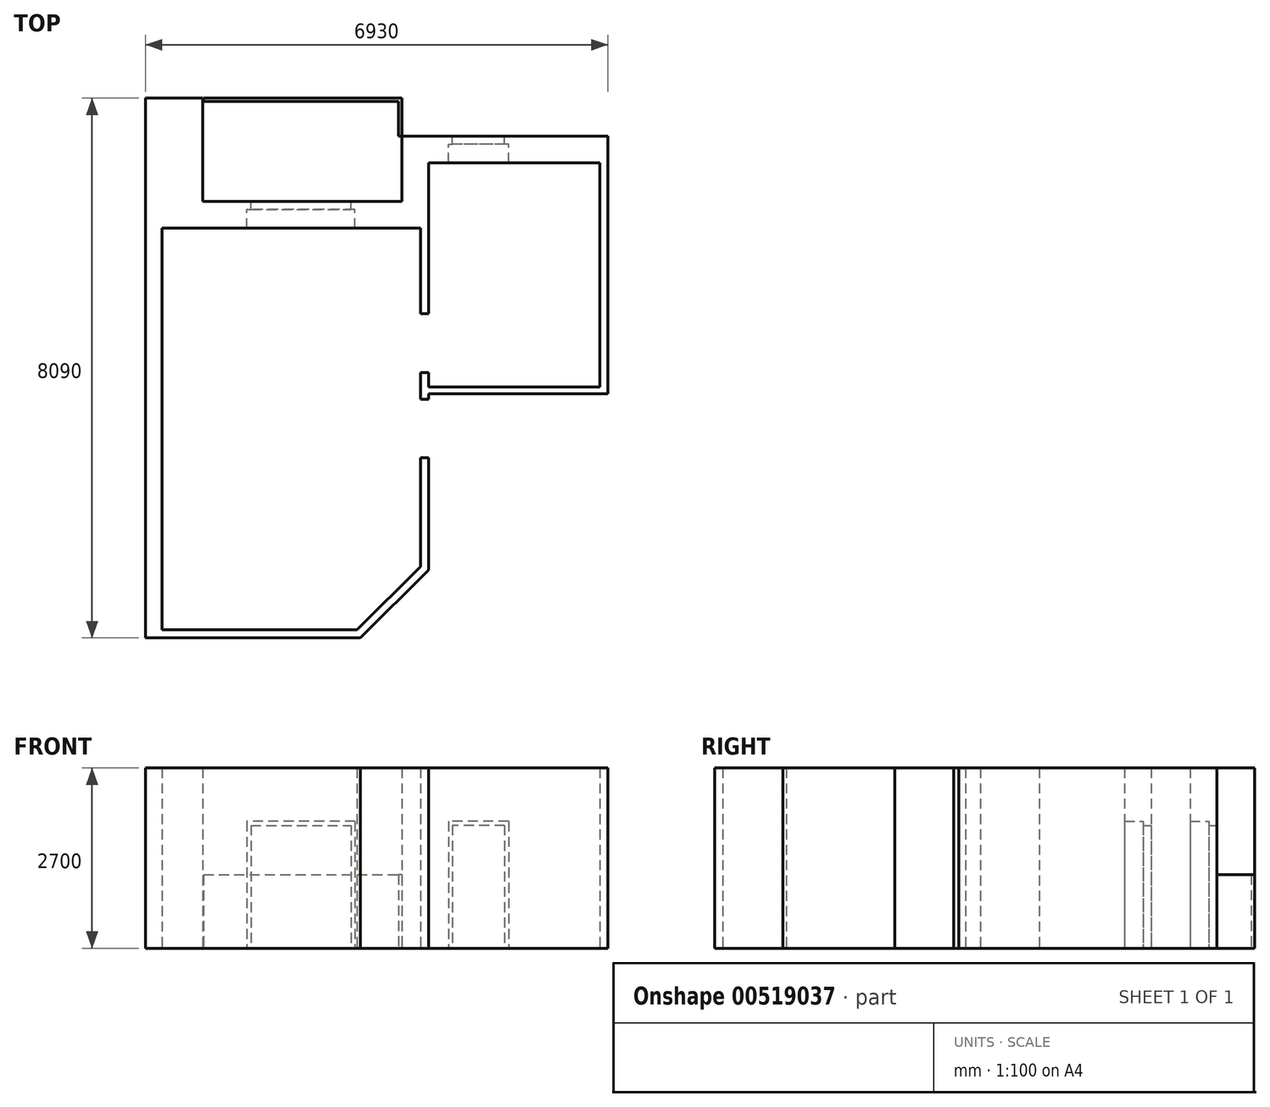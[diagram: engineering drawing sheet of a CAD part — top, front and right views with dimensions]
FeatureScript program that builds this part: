
annotation { "Feature Type Name" : "Feature", "Feature Type Description" : "" }
export const myFeature = defineFeature(function(context is Context, id is Id, definition is map)
    precondition{}
    {
        {
            var Q0;
            Q0=qCreatedBy(makeId("Top.planeOp"),FACE);
            var sketch = newSketch(context, id + "F0", { "sketchPlane" : qUnion([Q0])});
            skLineSegment(sketch, "E0", {"start": v(0, 0) * mm, "end": v(0, -6020) * mm, "construction": true});
            skLineSegment(sketch, "E1", {"start": v(0, -6020) * mm, "end": v(2920, -6020) * mm, "construction": true});
            skLineSegment(sketch, "E2", {"start": v(2920, -6020) * mm, "end": v(3870, -5070) * mm, "construction": true});
            skLineSegment(sketch, "E3", {"start": v(3870, -5070) * mm, "end": v(3870, 0) * mm, "construction": true});
            skLineSegment(sketch, "E4", {"start": v(3870, 0) * mm, "end": v(0, 0) * mm, "construction": true});
            skLineSegment(sketch, "E5.bottom", {"start": v(3990, 980) * mm, "end": v(6560, 980) * mm, "construction": true});
            skLineSegment(sketch, "E5.top", {"start": v(3990, -2380) * mm, "end": v(6560, -2380) * mm, "construction": true});
            skLineSegment(sketch, "E5.left", {"start": v(3990, 980) * mm, "end": v(3990, -2380) * mm, "construction": true});
            skLineSegment(sketch, "E5.right", {"start": v(6560, 980) * mm, "end": v(6560, -2380) * mm, "construction": true});
            skSolve(sketch);
        }
        {
            var Q0;
            Q0=qCreatedBy(makeId("Top.planeOp"),FACE);
            var sketch = newSketch(context, id + "F1", { "sketchPlane" : qUnion([Q0])});
            skLineSegment(sketch, "E6.0", {"start": v(0, 0) * mm, "end": v(0, -6020) * mm});
            skLineSegment(sketch, "E6.1", {"start": v(0, -6020) * mm, "end": v(2920, -6020) * mm});
            skLineSegment(sketch, "E6.2", {"start": v(2920, -6020) * mm, "end": v(3870, -5070) * mm});
            skLineSegment(sketch, "E6.3", {"start": v(3990, -2380) * mm, "end": v(6560, -2380) * mm});
            skLineSegment(sketch, "E6.4", {"start": v(6560, 980) * mm, "end": v(6560, -2380) * mm});
            skLineSegment(sketch, "E7", {"start": v(0, 0) * mm, "end": v(1270, 0) * mm});
            skLineSegment(sketch, "E8", {"start": v(1270, 0) * mm, "end": v(1270, 280) * mm});
            skLineSegment(sketch, "E9", {"start": v(1270, 280) * mm, "end": v(1330, 280) * mm});
            skLineSegment(sketch, "E10", {"start": v(1330, 280) * mm, "end": v(1330, 400) * mm});
            skLineSegment(sketch, "E11", {"start": v(2080, 0) * mm, "end": v(2080, 400) * mm, "construction": true});
            skLineSegment(sketch, "E12.MirrorCS", {"start": v(2890, 0) * mm, "end": v(2890, 280) * mm});
            skLineSegment(sketch, "E13.MirrorCS", {"start": v(2890, 280) * mm, "end": v(2830, 280) * mm});
            skLineSegment(sketch, "E14.MirrorCS", {"start": v(2830, 280) * mm, "end": v(2830, 400) * mm});
            skLineSegment(sketch, "E15", {"start": v(2890, 0) * mm, "end": v(3870, 0) * mm});
            skLineSegment(sketch, "E16", {"start": v(2830, 400) * mm, "end": v(3590, 400) * mm});
            skLineSegment(sketch, "E17", {"start": v(3590, 400) * mm, "end": v(3590, 1380) * mm});
            skLineSegment(sketch, "E18", {"start": v(3590, 1380) * mm, "end": v(4350, 1380) * mm});
            skLineSegment(sketch, "E19", {"start": v(3590, 1950) * mm, "end": v(3590, 1380) * mm});
            skLineSegment(sketch, "E20", {"start": v(3870, 0) * mm, "end": v(3870, -1280) * mm});
            skLineSegment(sketch, "E21", {"start": v(3870, -1280) * mm, "end": v(3990, -1280) * mm});
            skLineSegment(sketch, "E22", {"start": v(3990, -1280) * mm, "end": v(3990, 980) * mm});
            skLineSegment(sketch, "E23", {"start": v(3990, 980) * mm, "end": v(4290, 980) * mm});
            skLineSegment(sketch, "E24", {"start": v(4290, 980) * mm, "end": v(4290, 1260) * mm});
            skLineSegment(sketch, "E25", {"start": v(4290, 1260) * mm, "end": v(4350, 1260) * mm});
            skLineSegment(sketch, "E26", {"start": v(4350, 1260) * mm, "end": v(4350, 1380) * mm});
            skLineSegment(sketch, "E27", {"start": v(3870, -2560) * mm, "end": v(3990, -2560) * mm});
            skLineSegment(sketch, "E28", {"start": v(3870, -2560) * mm, "end": v(3870, -2160) * mm});
            skLineSegment(sketch, "E29", {"start": v(3870, -2160) * mm, "end": v(3990, -2160) * mm});
            skLineSegment(sketch, "E30", {"start": v(3990, -2160) * mm, "end": v(3990, -2380) * mm});
            skLineSegment(sketch, "E31", {"start": v(3990, -2560) * mm, "end": v(3990, -2482.77) * mm});
            skLineSegment(sketch, "E32", {"start": v(4740, 983.64) * mm, "end": v(4740, 1358.16) * mm, "construction": true});
            skLineSegment(sketch, "E33.MirrorCS", {"start": v(5130, 1260) * mm, "end": v(5130, 1380) * mm});
            skLineSegment(sketch, "E34.MirrorCS", {"start": v(5190, 980) * mm, "end": v(5190, 1260) * mm});
            skLineSegment(sketch, "E35.MirrorCS", {"start": v(5190, 1260) * mm, "end": v(5130, 1260) * mm});
            skLineSegment(sketch, "E36", {"start": v(5190, 980) * mm, "end": v(6560, 980) * mm});
            skLineSegment(sketch, "E37", {"start": v(5130, 1380) * mm, "end": v(6680, 1380) * mm});
            skLineSegment(sketch, "E38", {"start": v(6680, 1380) * mm, "end": v(6680, -2482.77) * mm});
            skLineSegment(sketch, "E39", {"start": v(3990, -2482.77) * mm, "end": v(6680, -2482.77) * mm});
            skLineSegment(sketch, "E40", {"start": v(3870, -5070) * mm, "end": v(3870, -3440) * mm});
            skLineSegment(sketch, "E41", {"start": v(3870, -3440) * mm, "end": v(3990, -3440) * mm});
            skLineSegment(sketch, "E42.0", {"start": v(3990, -5119.7) * mm, "end": v(3990, -3440) * mm});
            skLineSegment(sketch, "E42.1", {"start": v(2969.7, -6140) * mm, "end": v(3990, -5119.7) * mm});
            skLineSegment(sketch, "E42.2", {"start": v(-250, -6140) * mm, "end": v(2969.7, -6140) * mm});
            skLineSegment(sketch, "E43.0", {"start": v(-250, 1950) * mm, "end": v(-250, -6140) * mm});
            skLineSegment(sketch, "E44", {"start": v(-250, 1950) * mm, "end": v(610, 1950) * mm});
            skLineSegment(sketch, "E45", {"start": v(610, 1950) * mm, "end": v(610, 400) * mm});
            skLineSegment(sketch, "E46", {"start": v(610, 400) * mm, "end": v(1330, 400) * mm});
            skLineSegment(sketch, "E47.0", {"start": v(3540, 1900) * mm, "end": v(3540, 1380) * mm});
            skLineSegment(sketch, "E47.1", {"start": v(620, 1900) * mm, "end": v(3540, 1900) * mm});
            skLineSegment(sketch, "E48", {"start": v(3590, 1380) * mm, "end": v(3540, 1380) * mm});
            skLineSegment(sketch, "E49", {"start": v(620, 1900) * mm, "end": v(620, 1950) * mm});
            skLineSegment(sketch, "E50", {"start": v(620, 1950) * mm, "end": v(3590, 1950) * mm});
            skSolve(sketch);
        }
        {
            var Q0;
            Q0=makeQuery(id+"F1.imprint","IMPRINT",FACE,{"disambiguationData":[TD([[makeQuery(id+"F1.imprint","IMPRINT",EDGE,{"derivedFrom":sQuery(id+"F1.wireOp",EDGE,"E6.0")}),-1.0]])]});
            var Q1;
            Q1=makeQuery(id+"F1.imprint","IMPRINT",FACE,{"disambiguationData":[TD([[makeQuery(id+"F1.imprint","IMPRINT",EDGE,{"derivedFrom":sQuery(id+"F1.wireOp",EDGE,"E12.MirrorCS")}),-1.0]])]});
            var Q2;
            Q2=makeQuery(id+"F1.imprint","IMPRINT",FACE,{"disambiguationData":[TD([[makeQuery(id+"F1.imprint","IMPRINT",EDGE,{"derivedFrom":sQuery(id+"F1.wireOp",EDGE,"E6.3")}),-1.0]])]});
            extrude(context, id + "F2", {"entities" : qUnion([Q0, Q1, Q2]), "depth" : 2700 * mm, "offsetDistance" : 25 * mm});
        }
        {
            var Q0;
            Q0=makeQuery(id+"F1.imprint","IMPRINT",FACE,{"disambiguationData":[TD([[makeQuery(id+"F1.imprint","IMPRINT",EDGE,{"derivedFrom":sQuery(id+"F1.wireOp",EDGE,"E19")}),-1.0]])]});
            extrude(context, id + "F3", {"entities" : qUnion([Q0]), "depth" : 1100 * mm, "offsetDistance" : 25 * mm});
        }
        {
            var Q0;
            Q0=makeQuery(id+"F2.opExtrude","CAP_FACE",FACE,{"disambiguationData":[OSD([sQuery(id+"F1.wireOp",EDGE,"E6.0"),sQuery(id+"F1.wireOp",EDGE,"E6.1"),sQuery(id+"F1.wireOp",EDGE,"E6.2"),sQuery(id+"F1.wireOp",EDGE,"E7"),sQuery(id+"F1.wireOp",EDGE,"E8"),sQuery(id+"F1.wireOp",EDGE,"E9"),sQuery(id+"F1.wireOp",EDGE,"E10"),sQuery(id+"F1.wireOp",EDGE,"E40"),sQuery(id+"F1.wireOp",EDGE,"E41"),sQuery(id+"F1.wireOp",EDGE,"E42.0"),sQuery(id+"F1.wireOp",EDGE,"E42.1"),sQuery(id+"F1.wireOp",EDGE,"E42.2"),sQuery(id+"F1.wireOp",EDGE,"E43.0"),sQuery(id+"F1.wireOp",EDGE,"E44"),sQuery(id+"F1.wireOp",EDGE,"E45"),sQuery(id+"F1.wireOp",EDGE,"E46")])],"isStart":false});
            var sketch = newSketch(context, id + "F4", { "sketchPlane" : qUnion([Q0])});
            skLineSegment(sketch, "E51.0", {"start": v(1330, 280) * mm, "end": v(1330, 400) * mm});
            skLineSegment(sketch, "E51.1", {"start": v(1270, 280) * mm, "end": v(1330, 280) * mm});
            skLineSegment(sketch, "E51.2", {"start": v(1270, 0) * mm, "end": v(1270, 280) * mm});
            skLineSegment(sketch, "E51.3", {"start": v(2890, 0) * mm, "end": v(2890, 280) * mm});
            skLineSegment(sketch, "E51.4", {"start": v(2890, 280) * mm, "end": v(2830, 280) * mm});
            skLineSegment(sketch, "E51.5", {"start": v(2830, 280) * mm, "end": v(2830, 400) * mm});
            skLineSegment(sketch, "E52", {"start": v(1330, 400) * mm, "end": v(2830, 400) * mm});
            skLineSegment(sketch, "E53", {"start": v(1270, 0) * mm, "end": v(2890, 0) * mm});
            skLineSegment(sketch, "E54.0", {"start": v(4350, 1260) * mm, "end": v(4350, 1380) * mm});
            skLineSegment(sketch, "E54.1", {"start": v(4290, 1260) * mm, "end": v(4350, 1260) * mm});
            skLineSegment(sketch, "E54.2", {"start": v(4290, 980) * mm, "end": v(4290, 1260) * mm});
            skLineSegment(sketch, "E54.3", {"start": v(5130, 1260) * mm, "end": v(5130, 1380) * mm});
            skLineSegment(sketch, "E54.4", {"start": v(5190, 1260) * mm, "end": v(5130, 1260) * mm});
            skLineSegment(sketch, "E54.5", {"start": v(5190, 980) * mm, "end": v(5190, 1260) * mm});
            skLineSegment(sketch, "E55", {"start": v(5130, 1380) * mm, "end": v(4350, 1380) * mm});
            skLineSegment(sketch, "E56", {"start": v(4290, 980) * mm, "end": v(5190, 980) * mm});
            skSolve(sketch);
        }
        {
            var Q0;
            Q0=qSketchRegion(id+"F4",true);
            extrude(context, id + "F5", {"entities" : qUnion([Q0]), "operationType" : NewBodyOperationType.ADD, "oppositeDirection" : true, "depth" : 800 * mm, "offsetDistance" : 25 * mm});
        }
        {
            var Q0;
            Q0=makeQuery(id+"F5.opExtrude","CAP_FACE",FACE,{"disambiguationData":[OSD([sQuery(id+"F4.wireOp",EDGE,"E51.0"),sQuery(id+"F4.wireOp",EDGE,"E51.1"),sQuery(id+"F4.wireOp",EDGE,"E51.2"),sQuery(id+"F4.wireOp",EDGE,"E51.3"),sQuery(id+"F4.wireOp",EDGE,"E51.4"),sQuery(id+"F4.wireOp",EDGE,"E51.5"),sQuery(id+"F4.wireOp",EDGE,"E52"),sQuery(id+"F4.wireOp",EDGE,"E53")])],"isStart":false});
            var sketch = newSketch(context, id + "F6", { "sketchPlane" : qUnion([Q0])});
            skLineSegment(sketch, "E57.bottom", {"start": v(1330, -280) * mm, "end": v(2830, -280) * mm});
            skLineSegment(sketch, "E57.top", {"start": v(1330, -400) * mm, "end": v(2830, -400) * mm});
            skLineSegment(sketch, "E57.left", {"start": v(1330, -280) * mm, "end": v(1330, -400) * mm});
            skLineSegment(sketch, "E57.right", {"start": v(2830, -280) * mm, "end": v(2830, -400) * mm});
            skLineSegment(sketch, "E58.bottom", {"start": v(5130, -1260) * mm, "end": v(4350, -1260) * mm});
            skLineSegment(sketch, "E58.top", {"start": v(5130, -1380) * mm, "end": v(4350, -1380) * mm});
            skLineSegment(sketch, "E58.left", {"start": v(5130, -1260) * mm, "end": v(5130, -1380) * mm});
            skLineSegment(sketch, "E58.right", {"start": v(4350, -1260) * mm, "end": v(4350, -1380) * mm});
            skSolve(sketch);
        }
        {
            var Q0;
            Q0=qSketchRegion(id+"F6",true);
            extrude(context, id + "F7", {"entities" : qUnion([Q0]), "operationType" : NewBodyOperationType.ADD, "depth" : 60 * mm, "offsetDistance" : 25 * mm});
        }
    });
